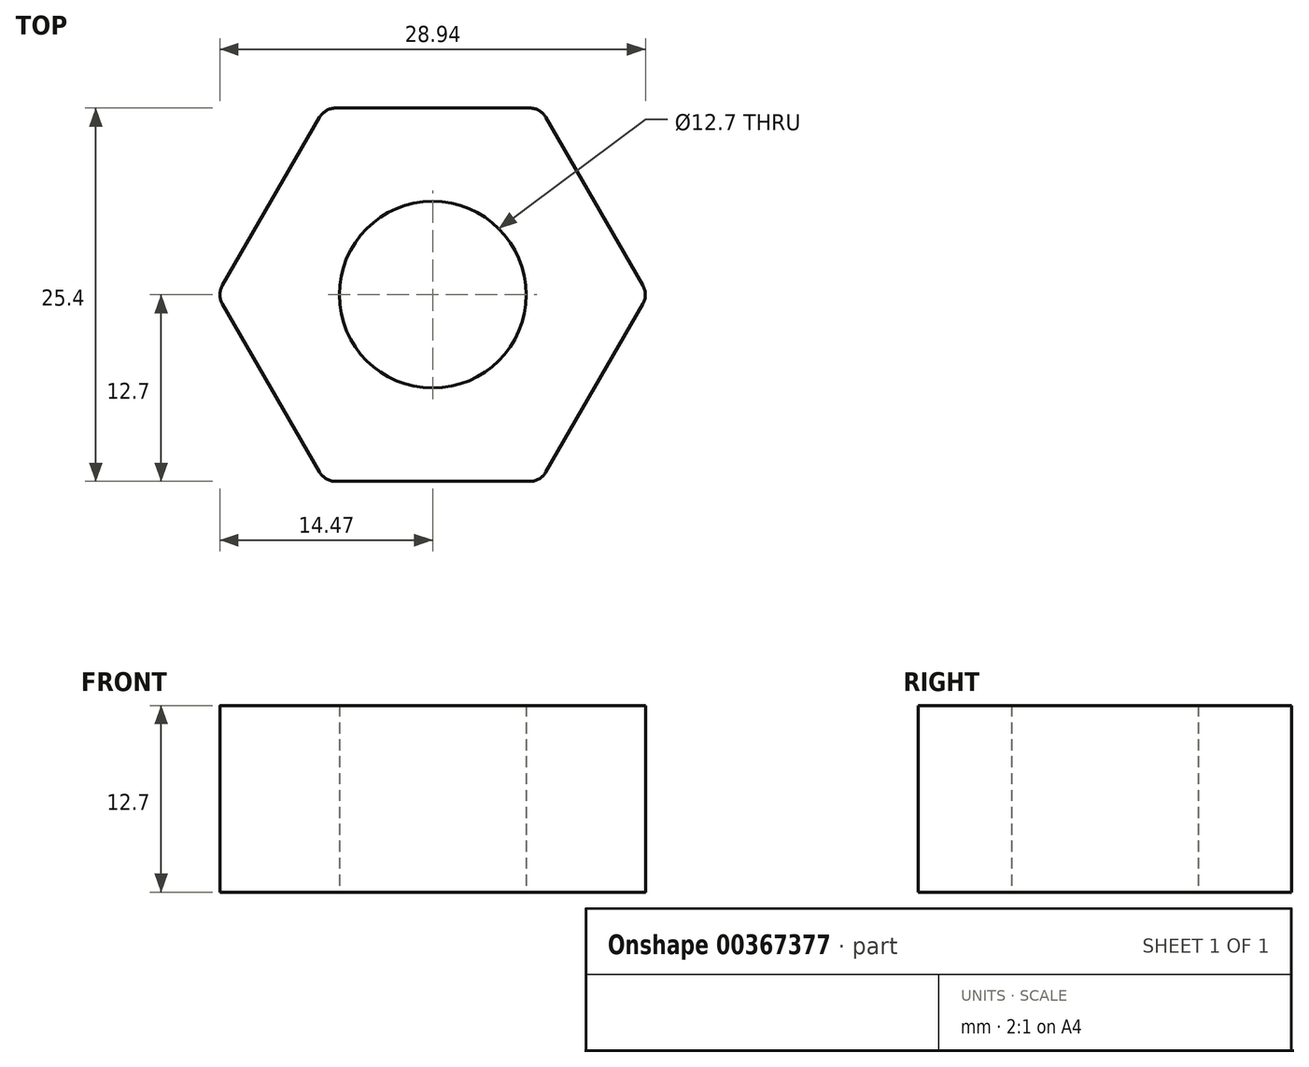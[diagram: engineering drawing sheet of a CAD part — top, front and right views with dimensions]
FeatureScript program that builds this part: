
annotation { "Feature Type Name" : "Feature", "Feature Type Description" : "" }
export const myFeature = defineFeature(function(context is Context, id is Id, definition is map)
    precondition{}
    {
        {
            var Q0;
            Q0=qCreatedBy(makeId("Top.planeOp"),FACE);
            var sketch = newSketch(context, id + "F0", { "sketchPlane" : qUnion([Q0])});
            skLineSegment(sketch, "E0", {"start": v(-7.33, 12.7) * mm, "end": v(7.33, 12.7) * mm});
            skLineSegment(sketch, "E1", {"start": v(7.33, 12.7) * mm, "end": v(14.66, 0) * mm});
            skLineSegment(sketch, "E2", {"start": v(14.66, 0) * mm, "end": v(7.33, -12.7) * mm});
            skLineSegment(sketch, "E3", {"start": v(7.33, -12.7) * mm, "end": v(-7.33, -12.7) * mm});
            skLineSegment(sketch, "E4", {"start": v(-7.33, -12.7) * mm, "end": v(-14.66, 0) * mm});
            skLineSegment(sketch, "E5", {"start": v(-14.66, 0) * mm, "end": v(-7.33, 12.7) * mm});
            skCircle(sketch, "E6", {"center": v(0, 0) * mm, "radius": 12.7 * mm, "construction": true});
            skCircle(sketch, "E7", {"center": v(0, 0) * mm, "radius": 6.35 * mm});
            skSolve(sketch);
        }
        {
            var Q0;
            Q0 = qSketchRegion(id + "F0", true);
            extrude(context, id + "F1", {"entities" : qUnion([Q0]), "depth" : 12.7 * mm});
        }
        {
            var Q0;
            Q0=makeQuery(id+"F1.opExtrude","SWEPT_EDGE",EDGE,{"disambiguationData":[OSD([sQuery(id+"F0.wireOp",EDGE,"E4"),sQuery(id+"F0.wireOp",EDGE,"E5")])]});
            var Q1;
            Q1=makeQuery(id+"F1.opExtrude","SWEPT_EDGE",EDGE,{"disambiguationData":[OSD([sQuery(id+"F0.wireOp",EDGE,"E0"),sQuery(id+"F0.wireOp",EDGE,"E5")])]});
            var Q2;
            Q2=makeQuery(id+"F1.opExtrude","SWEPT_EDGE",EDGE,{"disambiguationData":[OSD([sQuery(id+"F0.wireOp",EDGE,"E0"),sQuery(id+"F0.wireOp",EDGE,"E1")])]});
            var Q3;
            Q3=makeQuery(id+"F1.opExtrude","SWEPT_EDGE",EDGE,{"disambiguationData":[OSD([sQuery(id+"F0.wireOp",EDGE,"E1"),sQuery(id+"F0.wireOp",EDGE,"E2")])]});
            var Q4;
            Q4=makeQuery(id+"F1.opExtrude","SWEPT_EDGE",EDGE,{"disambiguationData":[OSD([sQuery(id+"F0.wireOp",EDGE,"E2"),sQuery(id+"F0.wireOp",EDGE,"E3")])]});
            var Q5;
            Q5=makeQuery(id+"F1.opExtrude","SWEPT_EDGE",EDGE,{"disambiguationData":[OSD([sQuery(id+"F0.wireOp",EDGE,"E3"),sQuery(id+"F0.wireOp",EDGE,"E4")])]});
            fillet(context, id + "F2", {"entities" : qUnion([Q0, Q1, Q2, Q3, Q4, Q5]), "radius" : 1.27 * mm, "tangentPropagation" : true, "allowEdgeOverflow" : false});
        }
    });
